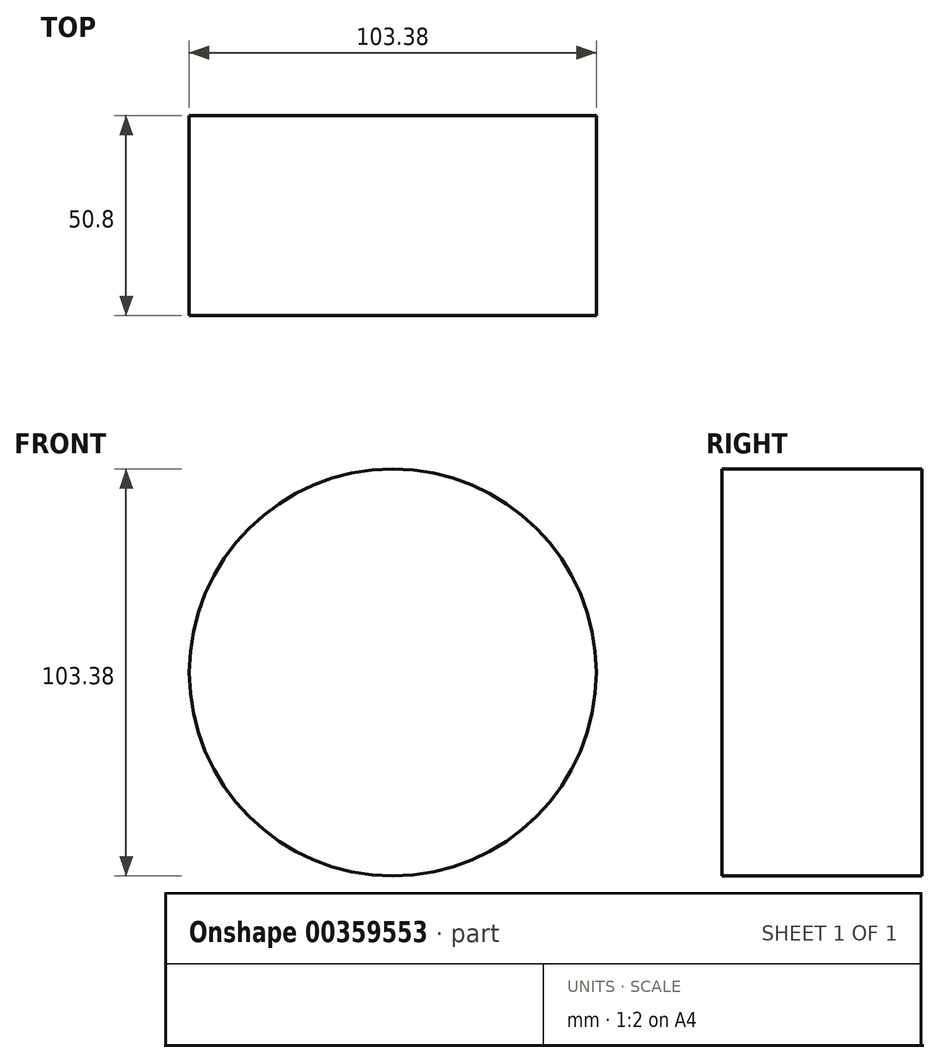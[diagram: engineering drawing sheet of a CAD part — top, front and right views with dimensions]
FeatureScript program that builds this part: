
annotation { "Feature Type Name" : "Feature", "Feature Type Description" : "" }
export const myFeature = defineFeature(function(context is Context, id is Id, definition is map)
    precondition{}
    {
        {
            var Q0;
            Q0=qCreatedBy(makeId("Front.planeOp"),FACE);
            var sketch = newSketch(context, id + "F0", { "sketchPlane" : qUnion([Q0])});
            skCircle(sketch, "E0", {"center": v(-18.54, 13.83) * mm, "radius": 51.7 * mm});
            skSolve(sketch);
        }
        {
            var Q0;
            Q0=sQuery(id+"F0.wireOp",EDGE,"E0");
            extrude(context, id + "F1", {"bodyType" : ToolBodyType.SURFACE, "surfaceEntities" : qUnion([Q0]), "depth" : 50.8 * mm});
        }
    });
